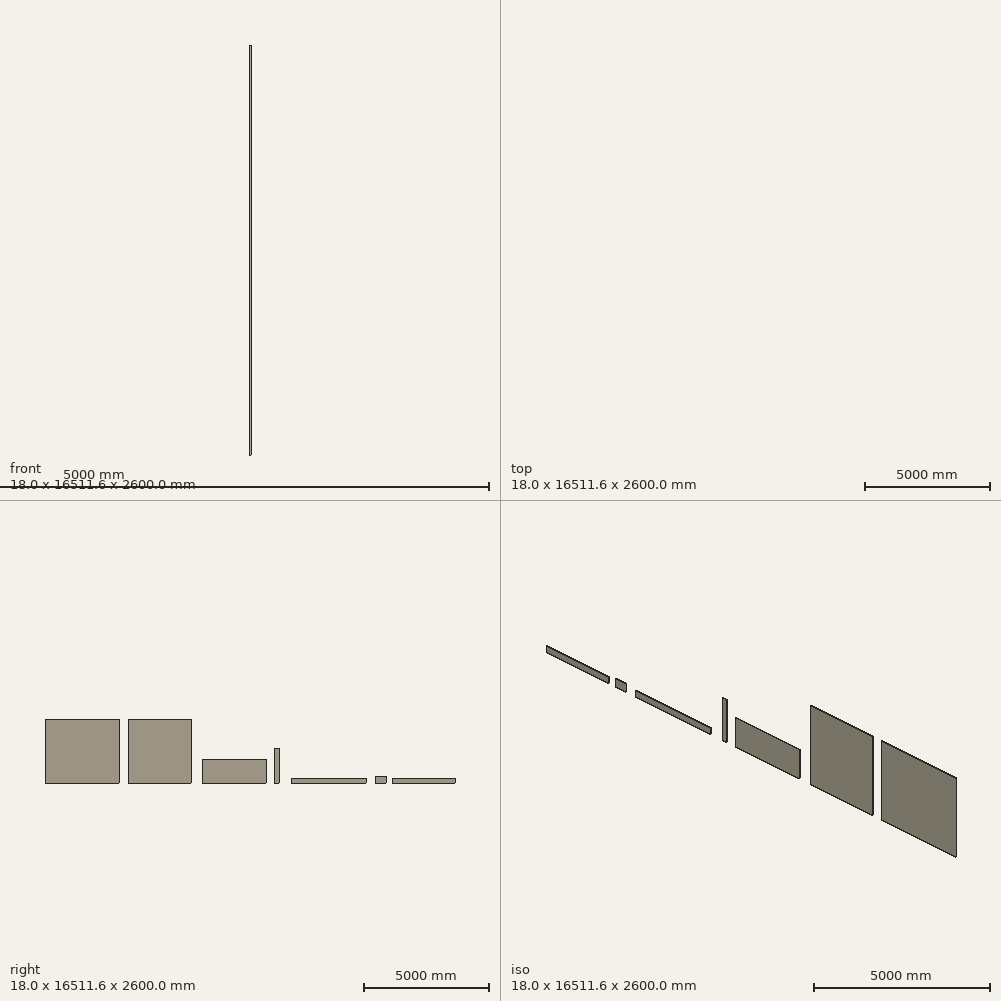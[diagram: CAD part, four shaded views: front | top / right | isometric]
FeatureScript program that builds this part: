
annotation { "Feature Type Name" : "Feature", "Feature Type Description" : "" }
export const myFeature = defineFeature(function(context is Context, id is Id, definition is map)
    precondition{}
    {
        {
            var Q0;
            Q0=qCreatedBy(makeId("Right.planeOp"),FACE);
            var sketch = newSketch(context, id + "F0", { "sketchPlane" : qUnion([Q0])});
            skLineSegment(sketch, "E0.bottom", {"start": v(0, 0) * mm, "end": v(2999.84, 0) * mm});
            skLineSegment(sketch, "E0.top", {"start": v(0, 2600) * mm, "end": v(2999.84, 2600) * mm});
            skLineSegment(sketch, "E0.left", {"start": v(0, 0) * mm, "end": v(0, 2600) * mm});
            skLineSegment(sketch, "E0.right", {"start": v(2999.84, 0) * mm, "end": v(2999.84, 2600) * mm});
            skSolve(sketch);
        }
        {
            var Q0;
            Q0 = qSketchRegion(id + "F0", true);
            extrude(context, id + "F1", {"entities" : qUnion([Q0]), "depth" : 18 * mm, "offsetDistance" : 25 * mm});
        }
        {
            var Q0;
            Q0=qCreatedBy(makeId("Right.planeOp"),FACE);
            var sketch = newSketch(context, id + "F2", { "sketchPlane" : qUnion([Q0])});
            skLineSegment(sketch, "E1.bottom", {"start": v(3362.13, 0) * mm, "end": v(5882.13, 0) * mm});
            skLineSegment(sketch, "E1.top", {"start": v(3362.13, 2600) * mm, "end": v(5882.13, 2600) * mm});
            skLineSegment(sketch, "E1.left", {"start": v(3362.13, 0) * mm, "end": v(3362.13, 2600) * mm});
            skLineSegment(sketch, "E1.right", {"start": v(5882.13, 0) * mm, "end": v(5882.13, 2600) * mm});
            skSolve(sketch);
        }
        {
            var Q0;
            Q0 = qSketchRegion(id + "F2", true);
            extrude(context, id + "F3", {"entities" : qUnion([Q0]), "depth" : 18 * mm, "offsetDistance" : 25 * mm});
        }
        {
            var Q0;
            Q0=qCreatedBy(makeId("Right.planeOp"),FACE);
            var sketch = newSketch(context, id + "F4", { "sketchPlane" : qUnion([Q0])});
            skLineSegment(sketch, "E2.bottom", {"start": v(6305.97, 0) * mm, "end": v(8885.97, 0) * mm});
            skLineSegment(sketch, "E2.top", {"start": v(6305.97, 965) * mm, "end": v(8885.97, 965) * mm});
            skLineSegment(sketch, "E2.left", {"start": v(6305.97, 0) * mm, "end": v(6305.97, 965) * mm});
            skLineSegment(sketch, "E2.right", {"start": v(8885.97, 0) * mm, "end": v(8885.97, 965) * mm});
            skSolve(sketch);
        }
        {
            var Q0;
            Q0=makeQuery(id+"F4.imprint","IMPRINT",FACE,{"disambiguationData":[TD([[makeQuery(id+"F4.imprint","IMPRINT",EDGE,{"derivedFrom":sQuery(id+"F4.wireOp",EDGE,"E2.bottom")}),1.0]])]});
            extrude(context, id + "F5", {"entities" : qUnion([Q0]), "depth" : 18 * mm, "offsetDistance" : 25 * mm});
        }
        {
            var Q0;
            Q0=qCreatedBy(makeId("Right.planeOp"),FACE);
            var sketch = newSketch(context, id + "F6", { "sketchPlane" : qUnion([Q0])});
            skLineSegment(sketch, "E3.bottom", {"start": v(9235.47, 0) * mm, "end": v(9425.47, 0) * mm});
            skLineSegment(sketch, "E3.top", {"start": v(9235.47, 1410) * mm, "end": v(9425.47, 1410) * mm});
            skLineSegment(sketch, "E3.left", {"start": v(9235.47, 0) * mm, "end": v(9235.47, 1410) * mm});
            skLineSegment(sketch, "E3.right", {"start": v(9425.47, 0) * mm, "end": v(9425.47, 1410) * mm});
            skSolve(sketch);
        }
        {
            var Q0;
            Q0=makeQuery(id+"F6.imprint","IMPRINT",FACE,{"disambiguationData":[TD([[makeQuery(id+"F6.imprint","IMPRINT",EDGE,{"derivedFrom":sQuery(id+"F6.wireOp",EDGE,"E3.bottom")}),1.0]])]});
            extrude(context, id + "F7", {"entities" : qUnion([Q0]), "depth" : 18 * mm, "offsetDistance" : 25 * mm});
        }
        {
            var Q0;
            Q0=qCreatedBy(makeId("Right.planeOp"),FACE);
            var sketch = newSketch(context, id + "F8", { "sketchPlane" : qUnion([Q0])});
            skLineSegment(sketch, "E4.bottom", {"start": v(9891.97, 0) * mm, "end": v(12909.97, 0) * mm});
            skLineSegment(sketch, "E4.top", {"start": v(9891.97, 220) * mm, "end": v(12909.97, 220) * mm});
            skLineSegment(sketch, "E4.left", {"start": v(9891.97, 0) * mm, "end": v(9891.97, 220) * mm});
            skLineSegment(sketch, "E4.right", {"start": v(12909.97, 0) * mm, "end": v(12909.97, 220) * mm});
            skSolve(sketch);
        }
        {
            var Q0;
            Q0 = qSketchRegion(id + "F8", true);
            extrude(context, id + "F9", {"entities" : qUnion([Q0]), "depth" : 18 * mm, "offsetDistance" : 25 * mm});
        }
        {
            var Q0;
            Q0=qCreatedBy(makeId("Right.planeOp"),FACE);
            var sketch = newSketch(context, id + "F10", { "sketchPlane" : qUnion([Q0])});
            skLineSegment(sketch, "E5.bottom", {"start": v(13289.56, 0) * mm, "end": v(13729.56, 0) * mm});
            skLineSegment(sketch, "E5.top", {"start": v(13289.56, 283) * mm, "end": v(13729.56, 283) * mm});
            skLineSegment(sketch, "E5.left", {"start": v(13289.56, 0) * mm, "end": v(13289.56, 283) * mm});
            skLineSegment(sketch, "E5.right", {"start": v(13729.56, 0) * mm, "end": v(13729.56, 283) * mm});
            skSolve(sketch);
        }
        {
            var Q0;
            Q0 = qSketchRegion(id + "F10", true);
            extrude(context, id + "F11", {"entities" : qUnion([Q0]), "depth" : 18 * mm, "offsetDistance" : 25 * mm});
        }
        {
            var Q0;
            Q0=qCreatedBy(makeId("Right.planeOp"),FACE);
            var sketch = newSketch(context, id + "F12", { "sketchPlane" : qUnion([Q0])});
            skLineSegment(sketch, "E6.bottom", {"start": v(13993.56, 0) * mm, "end": v(16511.56, 0) * mm});
            skLineSegment(sketch, "E6.top", {"start": v(13993.56, 220) * mm, "end": v(16511.56, 220) * mm});
            skLineSegment(sketch, "E6.left", {"start": v(13993.56, 0) * mm, "end": v(13993.56, 220) * mm});
            skLineSegment(sketch, "E6.right", {"start": v(16511.56, 0) * mm, "end": v(16511.56, 220) * mm});
            skSolve(sketch);
        }
        {
            var Q0;
            Q0 = qSketchRegion(id + "F12", true);
            extrude(context, id + "F13", {"entities" : qUnion([Q0]), "depth" : 18 * mm, "offsetDistance" : 25 * mm});
        }
    });
